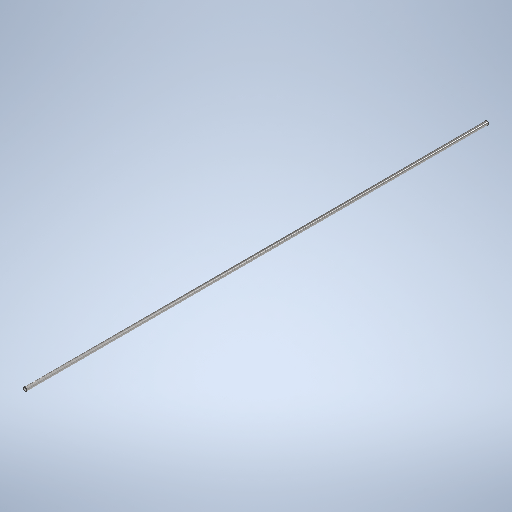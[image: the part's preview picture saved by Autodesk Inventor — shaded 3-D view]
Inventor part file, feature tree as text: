
AUTODESK INVENTOR PART (.ipt)
format: ipt  version: 2025.2 (Build 292293000, 293)  size: 245,248 bytes
history: native  units: mm
features: extrude x1, chamfer x1, sketch x1
ambient origin geometry x8: Origin, YZ Plane, XZ Plane, XY Plane, X Axis, Y Axis, Z Axis, Center Point
bodies: Solid1 (feature_tree)
feature tree (3):
  extrude  "Extrusion1"  Depth=1000.0mm TaperAngle=0.0deg
  chamfer  "Chamfer1"  Distance=0.5mm Angle=45.0deg
  sketch  "Sketch1"  dims[d0=8.0mm d1=1000.0mm d2=0.0mm d3=0.5mm d4=2.0mm d5=45.0deg]
